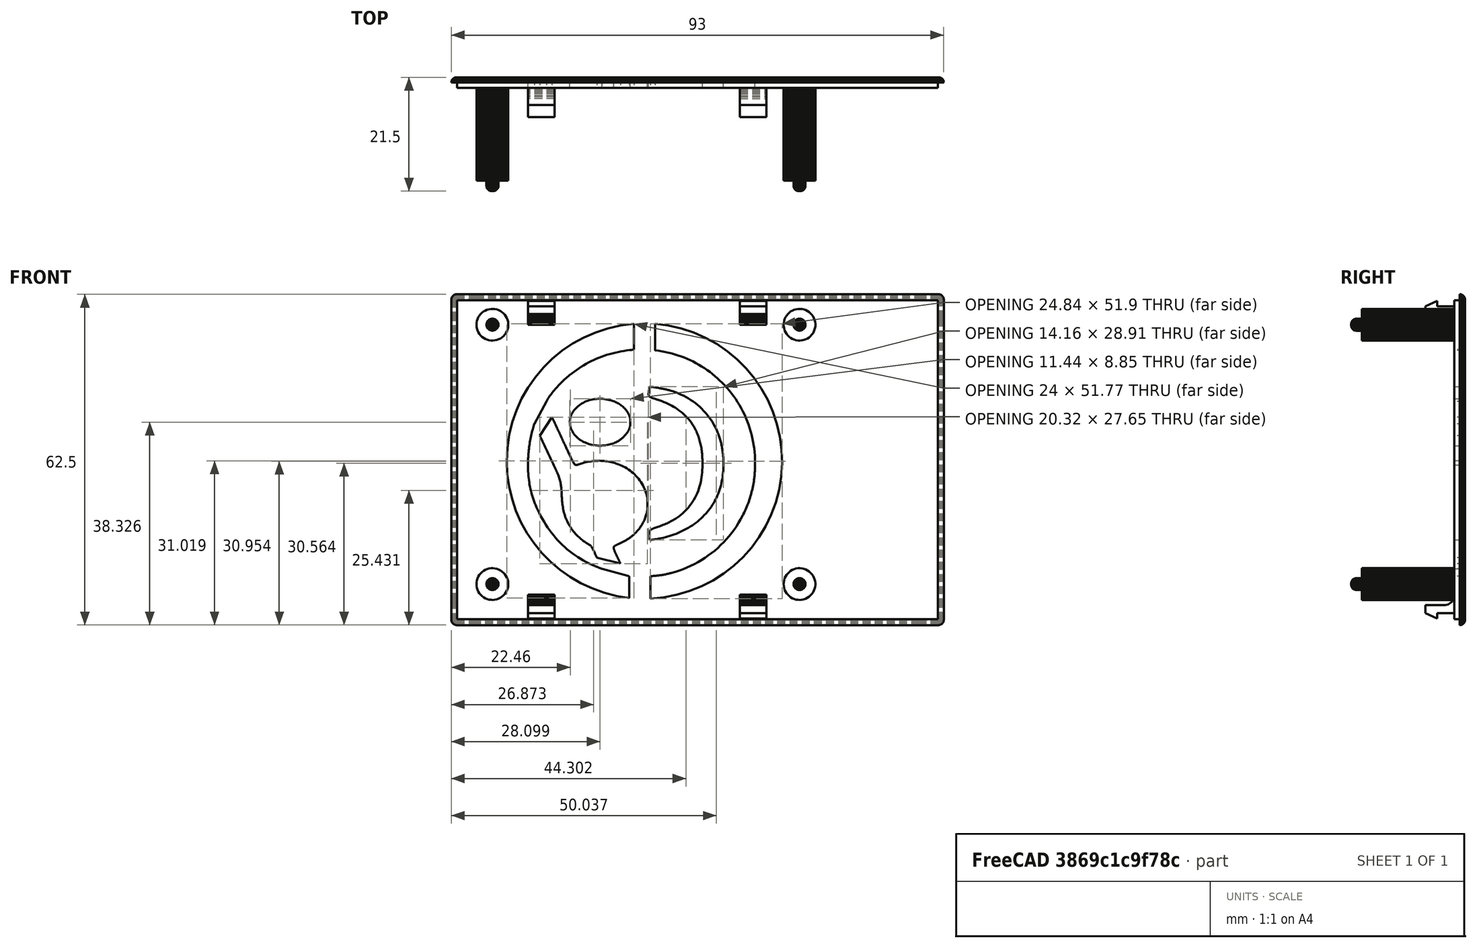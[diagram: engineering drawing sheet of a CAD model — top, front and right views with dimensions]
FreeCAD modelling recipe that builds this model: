
FCSTD DOCUMENT  (FreeCAD 0.18.4R)
Label: hackers_top
License: All rights reserved
LicenseURL: http://en.wikipedia.org/wiki/All_rights_reserved
objects: Part::Cut×6, Part::Feature×5, Part::Extrusion×5, Part::Compound×5, Part::Part2DObjectPython×4, Part::Face×1, Part::FeaturePython×1, Part::Cylinder×1
note: 28 computed .brp shape members not serialized (recipe doc carries the construction recipe); baked Part::Feature solids carry a one-line shape summary decoded from their .brp

FEATURE [Part::Feature] Wire
  shape: bbox 45.63 x 57.36 x 2e-07 mm, 0 faces, 0 solids (baked)
FEATURE [Part::Feature] Wire001
  shape: bbox 145.2 x 71.23 x 2e-07 mm, 0 faces, 0 solids (baked)
FEATURE [Part::Feature] Wire002
  shape: bbox 137.4 x 70.01 x 2e-07 mm, 0 faces, 0 solids (baked)
FEATURE [Part::Feature] Wire003
  shape: bbox 214.5 x 197.8 x 2e-07 mm, 0 faces, 0 solids (baked)
FEATURE [Part::Face] Face
  FaceMakerClass = Part::FaceMakerBullseye
  Sources = -> [Wire,Wire003,Wire002,Wire001]
FEATURE [Part::FeaturePython] Clone  label="Face001"  # Draft clone (typed FeaturePython)
  AttacherType = Attacher::AttachEngine3D
  Fuse = false
  Objects = -> [Face]
  Placement = pos=(0,0,0) rot=(-0.57735,-0.57735,0.57735;4.18879rad)
  Scale = (0.2,0.2,0.2)
FEATURE [Part::Extrusion] Extrude
  Base = -> Clone
  Dir = (0,-1,2e-16)
  DirMode = 2
  FaceMakerClass = Part::FaceMakerBullseye
  LengthFwd = 12
  LengthRev = 2
  Placement = pos=(-99,-5,21) rot=(0,0,1;0rad)
  Solid = false
  Symmetric = true
FEATURE [Part::Cylinder] Cylinder
  Angle = 360
  AttacherType = Attacher::AttachEngine3D
  Height = 10
  Placement = pos=(-120,0,0) rot=(1,0,0;1.5708rad)
  Radius = 26
FEATURE [Part::Cut] Cut
  Base = -> Cylinder
  Tool = -> Extrude
FEATURE [Part::Part2DObjectPython] Rectangle  # Draft 2D object (typed FeaturePython)
  ChamferSize = 0
  Columns = 1
  FilletRadius = 0
  Height = 12
  Length = 4
  MakeFace = false
  Placement = pos=(-122,0,18) rot=(1,0,0;1.5708rad)
  Rows = 1
FEATURE [Part::Part2DObjectPython] Rectangle001  # Draft 2D object (typed FeaturePython)
  ChamferSize = 0
  Columns = 1
  FilletRadius = 0
  Height = 12
  Length = 4
  MakeFace = false
  Placement = pos=(-121.157,0,-29.9393) rot=(1,0,0;1.5708rad)
  Rows = 1
FEATURE [Part::Extrusion] Extrude001
  Base = -> Rectangle
  Dir = (0,-1,2e-16)
  DirMode = 2
  FaceMakerClass = Part::FaceMakerBullseye
  LengthFwd = 10
  LengthRev = 0
  Solid = true
  Symmetric = false
FEATURE [Part::Extrusion] Extrude002
  Base = -> Rectangle001
  Dir = (0,-1,2e-16)
  DirMode = 2
  FaceMakerClass = Part::FaceMakerBullseye
  LengthFwd = 10
  LengthRev = 0
  Solid = true
  Symmetric = false
FEATURE [Part::Compound] Compound  label="PlainSmiley"
  Links = -> [Cut]
FEATURE [Part::Cut] Cut001
  Base = -> Compound
  Tool = -> Extrude002
FEATURE [Part::Compound] Compound001
  Links = -> [Cut001]
FEATURE [Part::Cut] Cut002
  Base = -> Compound001
  Tool = -> Extrude001
FEATURE [Part::Compound] Compound002
  Links = -> [Cut002]
FEATURE [Part::Part2DObjectPython] Wire004  # Draft 2D object (typed FeaturePython)
  ChamferSize = 0
  Closed = true
  End = (-102.556,-10,8.27751)
  FilletRadius = 0
  Length = 15.3676
  MakeFace = true
  Placement = pos=(-101.674,-10,11.6136) rot=(1,0,0;1.5708rad)
  Points = (4) [(0,0,0),(2.5475,-4.81776,0),(1.40607,-6.81659,0),(-0.882027,-3.33604,0)]
  Start = (-101.674,-10,11.6136)
  Subdivisions = 0
FEATURE [Part::Part2DObjectPython] Wire005  # Draft 2D object (typed FeaturePython)
  ChamferSize = 0
  Closed = true
  End = (-115.446,-10,-19.3284)
  FilletRadius = 0
  Length = 14.7331
  MakeFace = true
  Placement = pos=(-116.854,-10,-21.6921) rot=(1,0,0;1.5708rad)
  Points = (4) [(0,0,0),(5.05236,1.41453,0),(5.82973,3.45231,1.77636e-15),(1.40723,2.36375,1.06581e-14)]
  Start = (-116.854,-10,-21.6921)
  Subdivisions = 0
FEATURE [Part::Extrusion] Extrude003
  Base = -> Wire005
  Dir = (0,-1,2e-16)
  DirMode = 2
  FaceMakerClass = Part::FaceMakerBullseye
  LengthFwd = 0
  LengthRev = 10
  Solid = false
  Symmetric = false
FEATURE [Part::Extrusion] Extrude005
  Base = -> Wire004
  Dir = (0,-1,2e-16)
  DirMode = 2
  FaceMakerClass = Part::FaceMakerBullseye
  LengthFwd = 0
  LengthRev = 10
  Solid = false
  Symmetric = false
FEATURE [Part::Cut] Cut003
  Base = -> Compound002
  Tool = -> Extrude003
FEATURE [Part::Compound] Compound003
  Links = -> [Cut003]
FEATURE [Part::Cut] Cut004
  Base = -> Compound003
  Tool = -> Extrude005
FEATURE [Part::Compound] Compound004
  Links = -> [Cut004]
  Placement = pos=(-124,-5,6) rot=(0,0,1;3.14159rad)
FEATURE [Part::Feature] Solid
  shape: bbox 93 x 21.5 x 62.5 mm, 3953 faces (baked)
FEATURE [Part::Cut] Cut005
  Base = -> Solid
  Tool = -> Compound004
